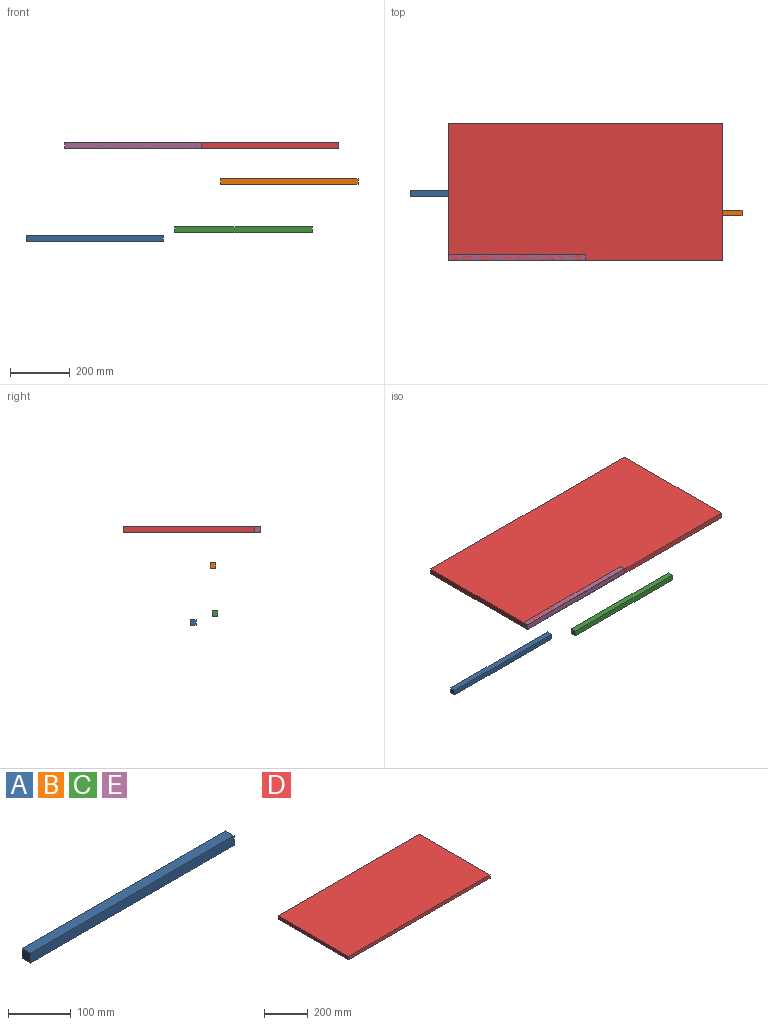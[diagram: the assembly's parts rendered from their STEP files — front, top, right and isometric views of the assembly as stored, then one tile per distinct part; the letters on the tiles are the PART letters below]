
ASSEMBLY  parts=5 mates=1
PART A: 6 faces, bbox 457.2x19.1x19.1 mm
  f0: plane 19.05x19.05mm, normal (-1,0,0), area 362.9mm2, adj f1,f3,f4,f5
  f1: plane 457.2x19.05mm, normal (0,0,-1), area 8709.7mm2, adj f0,f2,f4,f5
  f2: plane 19.05x19.05mm, normal (1,0,0), area 362.9mm2, adj f1,f3,f4,f5
  f3: plane 457.2x19.05mm, normal (0,0,1), area 8709.7mm2, adj f0,f2,f4,f5
  f4: plane 457.2x19.05mm, normal (0,-1,0), area 8709.7mm2, adj f0,f1,f2,f3
  f5: plane 457.2x19.05mm, normal (0,1,0), area 8709.7mm2, adj f0,f1,f2,f3
PART B: same geometry as A
PART C: same geometry as A
PART D: 6 faces, bbox 914.4x457.2x19.1 mm
  f0: plane 457.2x19.05mm, normal (-1,0,0), area 8709.7mm2, adj f1,f3,f4,f5
  f1: plane 914.4x19.05mm, normal (0,-1,0), area 17419.3mm2, adj f0,f2,f4,f5
  f2: plane 457.2x19.05mm, normal (1,0,0), area 8709.7mm2, adj f1,f3,f4,f5
  f3: plane 914.4x19.05mm, normal (0,1,0), area 17419.3mm2, adj f0,f2,f4,f5
  f4: plane 914.4x457.2mm, normal (0,0,1), area 418063.7mm2, adj f0,f1,f2,f3
  f5: plane 914.4x457.2mm, normal (0,0,-1), area 418063.7mm2, adj f0,f1,f2,f3
PART E: same geometry as A
PLACE A t=(-527.07,0.43,-423.46)mm
PLACE B t=(122.69,-65.12,-233.5)mm
PLACE C t=(-30.45,-72.35,-394.11)mm
PLACE D t=(-169.86,4.62,-113.58)mm fixed
PLACE E rot(axis=(0,1,0),180deg) t=(-398.46,-214.46,-113.58)mm
MATE fastened E.f3 <-> D.f5  axis (0,0,-1) through (-627.06,-223.98,-123.11)mm
